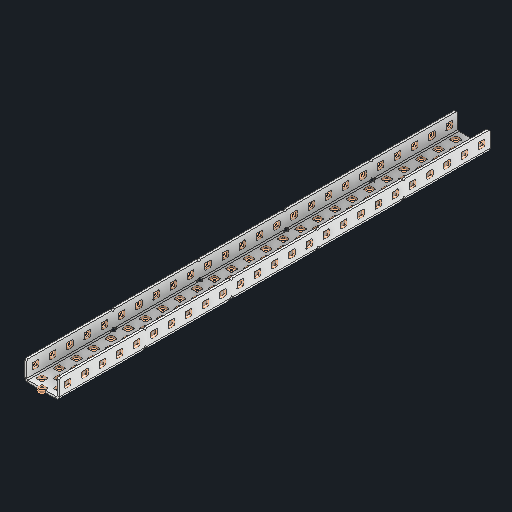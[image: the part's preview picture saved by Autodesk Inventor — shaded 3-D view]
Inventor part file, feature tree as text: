
AUTODESK INVENTOR PART (.ipt)
format: ipt  version: 2024 (Build 280153000, 153)  size: 2,045,952 bytes
history: native  units: in
note: dims shown in document units (in); Inventor stores cm internally (conversion verified against a paired STEP export)
features: other x256, sketch x5, sheet_metal_op x1
ambient origin geometry x8: Origin, YZ Plane, XZ Plane, XY Plane, X Axis, Y Axis, Z Axis, Center Point
bodies: Solid1 (feature_tree)
feature tree (262):
  other  "Alu C 1x2x1x25.ipt"
  other  "Solid1::Alu C 1x2x1x25.ipt"
  other  "TaggingFeature1"
  sketch  "Sketch1"  dims[d0=0.3937in]
  sketch  "Sketch2"  dims[d1=0.0625in]
  sketch  "Sketch3"
  other  "Flange Pattern Sketch"
  sketch  "Sketch9"
  sheet_metal_op  "Body Pattern Sketch"
  other  "Arc Length"
  sketch  "Sketch14"
  other  "Flange Pattern Plane"
  other  "Srf1"
  other  "Srf2"
  other  "Srf3"
  other  "Srf4"
  other  "Srf5"
  other  "Srf6"
  other  "Srf7"
  other  "Srf8"
  other  "Srf9"
  other  "Srf10"
  other  "Srf11"
  other  "Srf12"
  other  "Srf13"
  other  "Srf14"
  other  "Srf15"
  other  "Srf16"
  other  "Srf17"
  other  "Srf18"
  other  "Srf19"
  other  "Srf20"
  other  "Srf21"
  other  "Srf22"
  other  "Srf23"
  other  "Srf24"
  other  "Srf25"
  other  "Srf26"
  other  "Srf27"
  other  "Srf28"
  other  "Srf29"
  other  "Srf30"
  other  "Srf31"
  other  "Srf32"
  other  "Srf33"
  other  "Srf34"
  other  "Srf35"
  other  "Srf36"
  other  "Srf37"
  other  "Srf38"
  other  "Srf39"
  other  "Srf40"
  other  "Srf41"
  other  "Srf42"
  other  "Srf43"
  other  "Srf44"
  other  "Srf45"
  other  "Srf46"
  other  "Srf47"
  other  "Srf48"
  other  "Srf49"
  other  "Srf50"
  other  "Srf51"
  other  "Srf52"
  other  "Srf53"
  other  "Srf54"
  other  "Srf55"
  other  "Srf56"
  other  "Srf57"
  other  "Srf58"
  other  "Srf59"
  other  "Srf60"
  other  "Srf61"
  other  "Srf62"
  other  "Srf63"
  other  "Srf64"
  other  "Srf65"
  other  "Srf66"
  other  "Srf67"
  other  "Srf68"
  other  "Srf69"
  other  "Srf70"
  other  "Srf71"
  other  "Srf72"
  other  "Srf73"
  other  "Srf74"
  other  "Srf75"
  other  "Srf76"
  other  "Srf77"
  other  "Srf78"
  other  "Srf79"
  other  "Srf80"
  other  "Srf81"
  other  "Srf82"
  other  "Srf83"
  other  "Srf84"
  other  "Srf85"
  other  "Srf86"
  other  "Srf87"
  other  "Srf88"
  other  "Srf89"
  other  "Srf90"
  other  "Srf91"
  other  "Srf92"
  other  "Srf93"
  other  "Srf94"
  other  "Srf95"
  other  "Srf96"
  other  "Srf97"
  other  "Srf98"
  other  "Srf99"
  other  "Srf100"
  other  "Srf101"
  other  "Srf102"
  other  "Srf103"
  other  "Srf104"
  other  "Srf105"
  other  "Srf106"
  other  "Srf107"
  other  "Srf108"
  other  "Srf109"
  other  "Srf110"
  other  "Srf111"
  other  "Srf112"
  other  "Srf113"
  other  "Srf114"
  other  "Srf115"
  other  "Srf116"
  other  "Srf117"
  other  "Srf118"
  other  "Srf119"
  other  "Srf120"
  other  "Srf121"
  other  "Srf122"
  other  "Srf123"
  other  "Srf124"
  other  "Srf125"
  other  "Srf1::Derived"
  other  "Srf2::Derived"
  other  "Srf823::Derived"
  other  "Srf824::Derived"
  other  "Srf825::Derived"
  other  "Srf826::Derived"
  other  "Srf827::Derived"
  other  "Srf828::Derived"
  other  "Srf829::Derived"
  other  "Srf922::Derived"
  other  "Srf923::Derived"
  other  "Srf924::Derived"
  other  "Srf925::Derived"
  other  "Srf926::Derived"
  other  "Srf1143::Derived"
  other  "Srf1144::Derived"
  other  "Srf1145::Derived"
  other  "Srf1146::Derived"
  other  "Srf1147::Derived"
  other  "Srf1148::Derived"
  other  "Srf1149::Derived"
  other  "Srf1150::Derived"
  other  "Srf1151::Derived"
  other  "Srf1152::Derived"
  other  "Srf1153::Derived"
  other  "Srf1154::Derived"
  other  "Srf1155::Derived"
  other  "Srf1156::Derived"
  other  "Srf1157::Derived"
  other  "Srf1158::Derived"
  other  "Srf1159::Derived"
  other  "Srf1160::Derived"
  other  "Srf1161::Derived"
  other  "Srf1162::Derived"
  other  "Srf1163::Derived"
  other  "Srf1164::Derived"
  other  "Srf1165::Derived"
  other  "Srf1166::Derived"
  other  "Srf1167::Derived"
  other  "Srf1168::Derived"
  other  "Srf1169::Derived"
  other  "Srf1170::Derived"
  other  "Srf1171::Derived"
  other  "Srf1172::Derived"
  other  "Srf1173::Derived"
  other  "Srf1174::Derived"
  other  "Srf1175::Derived"
  other  "Srf1176::Derived"
  other  "Srf1177::Derived"
  other  "Srf1178::Derived"
  other  "Srf91::Derived"
  other  "Srf92::Derived"
  other  "Srf856::Derived"
  other  "Srf857::Derived"
  other  "Srf858::Derived"
  other  "Srf859::Derived"
  other  "Srf860::Derived"
  other  "Srf861::Derived"
  other  "Srf862::Derived"
  other  "Srf959::Derived"
  other  "Srf960::Derived"
  other  "Srf961::Derived"
  other  "Srf962::Derived"
  other  "Srf963::Derived"
  other  "Srf1199::Derived"
  other  "Srf1200::Derived"
  other  "Srf1201::Derived"
  other  "Srf1202::Derived"
  other  "Srf1203::Derived"
  other  "Srf1204::Derived"
  other  "Srf1205::Derived"
  other  "Srf1206::Derived"
  other  "Srf1207::Derived"
  other  "Srf1208::Derived"
  other  "Srf1209::Derived"
  other  "Srf1210::Derived"
  other  "Srf1211::Derived"
  other  "Srf1212::Derived"
  other  "Srf1213::Derived"
  other  "Srf1214::Derived"
  other  "Srf1215::Derived"
  other  "Srf1216::Derived"
  other  "Srf1217::Derived"
  other  "Srf1218::Derived"
  other  "Srf1219::Derived"
  other  "Srf1220::Derived"
  other  "Srf1221::Derived"
  other  "Srf1222::Derived"
  other  "Srf1223::Derived"
  other  "Srf1224::Derived"
  other  "Srf1225::Derived"
  other  "Srf1226::Derived"
  other  "Srf1227::Derived"
  other  "Srf1228::Derived"
  other  "Srf1229::Derived"
  other  "Srf1230::Derived"
  other  "Srf1231::Derived"
  other  "Srf1232::Derived"
  other  "Srf1233::Derived"
  other  "Srf1234::Derived"
  other  "Srf786::Derived"
  other  "Srf889::Derived"
  other  "Srf890::Derived"
  other  "Srf891::Derived"
  other  "Srf892::Derived"
  other  "Srf893::Derived"
  other  "Srf894::Derived"
  other  "Srf895::Derived"
  other  "Srf896::Derived"
  other  "Srf996::Derived"
  other  "Srf997::Derived"
  other  "Srf998::Derived"
  other  "Srf999::Derived"
  other  "Srf1000::Derived"
  other  "Srf1255::Derived"
  other  "Srf1256::Derived"
  other  "Srf1257::Derived"
  other  "Srf1258::Derived"
  other  "Srf1259::Derived"
  other  "Srf1260::Derived"
  other  "Srf1261::Derived"
  other  "Srf1262::Derived"
  other  "Srf1263::Derived"
  other  "Srf1264::Derived"
  other  "Srf1265::Derived"
